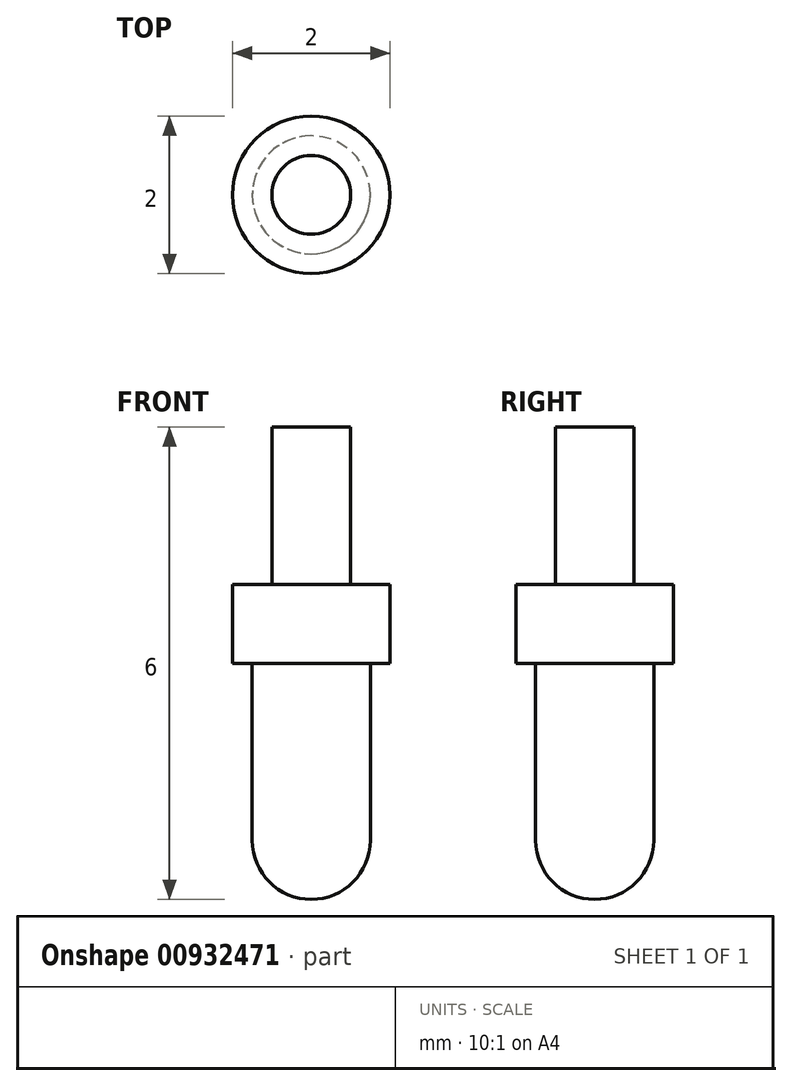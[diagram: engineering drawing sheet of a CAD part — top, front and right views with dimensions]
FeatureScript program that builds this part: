
annotation { "Feature Type Name" : "Feature", "Feature Type Description" : "" }
export const myFeature = defineFeature(function(context is Context, id is Id, definition is map)
    precondition{}
    {
        {
            var Q0;
            Q0=qCreatedBy(makeId("Top.planeOp"),FACE);
            var sketch = newSketch(context, id + "F0", { "sketchPlane" : qUnion([Q0])});
            skCircle(sketch, "E0", {"center": v(0, 0) * mm, "radius": 0.75 * mm});
            skLineSegment(sketch, "E1", {"start": v(0, 0.75) * mm, "end": v(0, -0.75) * mm});
            skArc(sketch, "E2", {"start": v(0, -0.75) * mm, "mid": v(0.75, 0) * mm, "end": v(0, 0.75) * mm});
            skSolve(sketch);
        }
        {
            var Q0;
            {var subQ0=sQuery(id+"F0.wireOp",EDGE,"E1");Q0=makeQuery(id+"F0.imprint","IMPRINT",FACE,{"disambiguationData":[TD([[makeQuery(id+"F0.imprint","IMPRINT",EDGE,{"derivedFrom":subQ0}),-1.0]])]});}
            var Q1;
            Q1=sQuery(id+"F0.wireOp",EDGE,"E1");
            revolve(context, id + "F1", {"surfaceOperationType" : NewSurfaceOperationType.NEW, "entities" : qUnion([Q0]), "axis" : qUnion([Q1]), "revolveType" : RevolveType.ONE_DIRECTION, "angle" : 180 * degree});
        }
        {
            var Q0;
            Q0 = qSketchRegion(id + "F0", true);
            extrude(context, id + "F2", {"entities" : qUnion([Q0]), "operationType" : NewBodyOperationType.ADD, "depth" : 2.25 * mm, "offsetDistance" : 25 * mm});
        }
        {
            var Q0;
            Q0=makeQuery(id+"F2.opExtrude","CAP_FACE",FACE,{"disambiguationData":[OSD([sQuery(id+"F0.wireOp",EDGE,"E0")])],"isStart":false});
            var sketch = newSketch(context, id + "F3", { "sketchPlane" : qUnion([Q0])});
            skCircle(sketch, "E3", {"center": v(0, 0) * mm, "radius": 1 * mm});
            skSolve(sketch);
        }
        {
            var Q0;
            Q0 = qSketchRegion(id + "F3", true);
            extrude(context, id + "F4", {"entities" : qUnion([Q0]), "operationType" : NewBodyOperationType.ADD, "depth" : 1 * mm, "offsetDistance" : 25 * mm});
        }
        {
            var Q0;
            Q0=makeQuery(id+"F4.opExtrude","CAP_FACE",FACE,{"disambiguationData":[OSD([sQuery(id+"F3.wireOp",EDGE,"E3")])],"isStart":false});
            var sketch = newSketch(context, id + "F5", { "sketchPlane" : qUnion([Q0])});
            skCircle(sketch, "E4", {"center": v(0, 0) * mm, "radius": 0.5 * mm});
            skSolve(sketch);
        }
        {
            var Q0;
            Q0=makeQuery(id+"F5.imprint","IMPRINT",FACE,{"disambiguationData":[TD([[makeQuery(id+"F5.imprint","IMPRINT",EDGE,{"derivedFrom":sQuery(id+"F5.wireOp",EDGE,"E4")}),1.0]])]});
            extrude(context, id + "F6", {"entities" : qUnion([Q0]), "operationType" : NewBodyOperationType.ADD, "depth" : 2 * mm, "offsetDistance" : 25 * mm});
        }
    });
